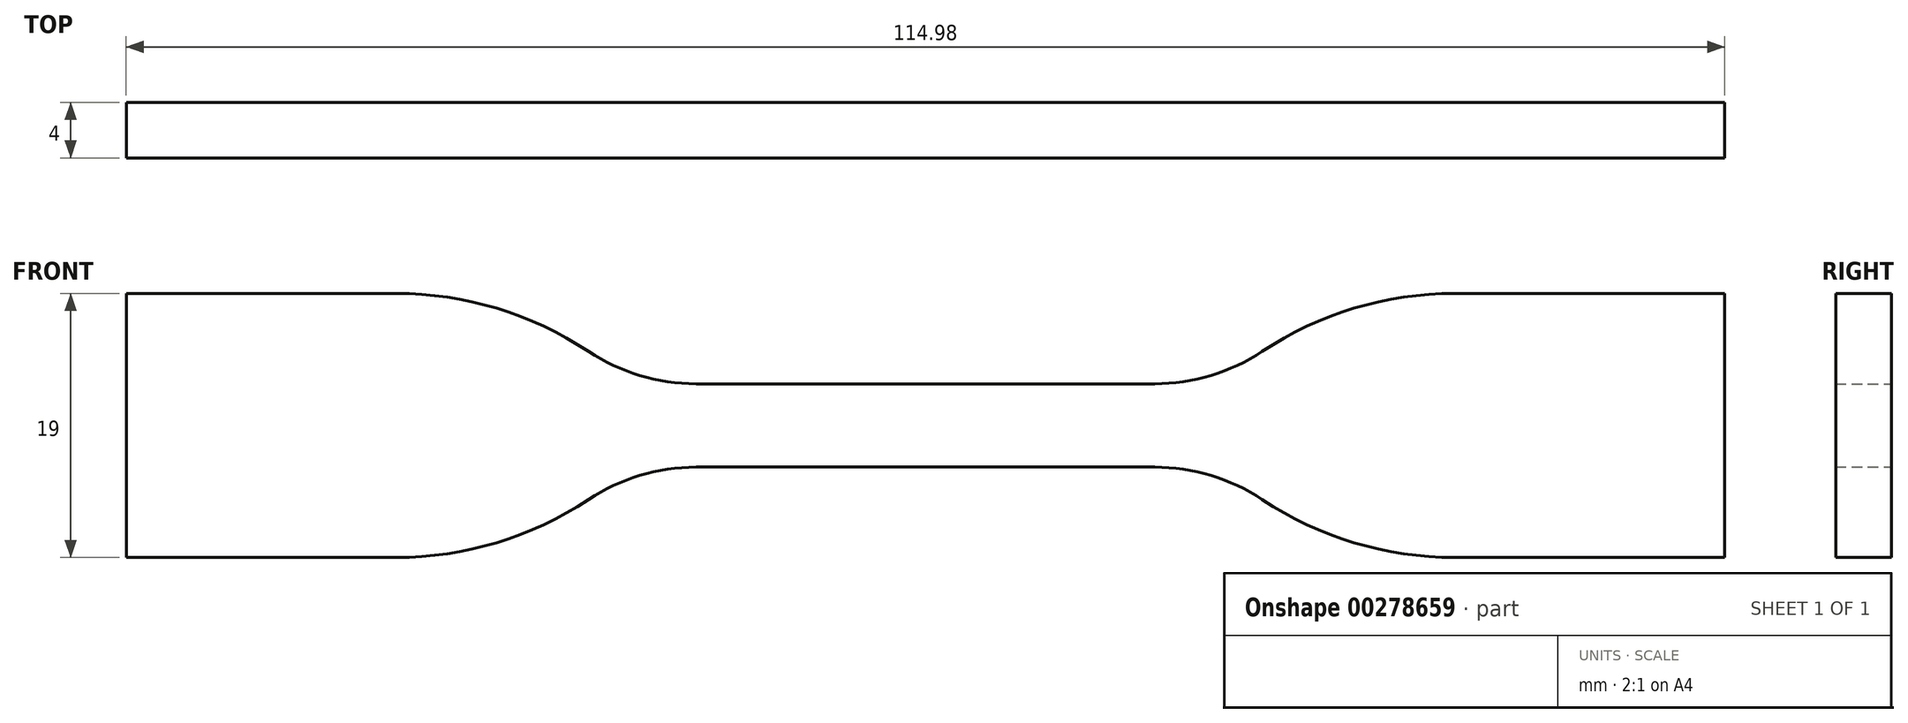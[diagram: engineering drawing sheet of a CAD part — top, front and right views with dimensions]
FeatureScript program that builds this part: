
annotation { "Feature Type Name" : "Feature", "Feature Type Description" : "" }
export const myFeature = defineFeature(function(context is Context, id is Id, definition is map)
    precondition{}
    {
        {
            var Q0;
            Q0=qCreatedBy(makeId("Front.planeOp"),FACE);
            var sketch = newSketch(context, id + "F0", { "sketchPlane" : qUnion([Q0])});
            skLineSegment(sketch, "E0", {"start": v(0, 3) * mm, "end": v(16.5, 3) * mm});
            skArc(sketch, "E1", {"start": v(16.5, 3) * mm, "mid": v(20.54, 3.6) * mm, "end": v(24.24, 5.33) * mm});
            skArc(sketch, "E2", {"start": v(24.24, 5.33) * mm, "mid": v(30.84, 8.43) * mm, "end": v(38.06, 9.5) * mm});
            skLineSegment(sketch, "E3", {"start": v(38.06, 9.5) * mm, "end": v(57.49, 9.5) * mm});
            skLineSegment(sketch, "E4.MirrorCS", {"start": v(0, -3) * mm, "end": v(16.5, -3) * mm});
            skLineSegment(sketch, "E5.MirrorCS", {"start": v(38.06, -9.5) * mm, "end": v(57.49, -9.5) * mm});
            skArc(sketch, "E6.MirrorCS", {"start": v(24.24, -5.33) * mm, "mid": v(30.84, -8.43) * mm, "end": v(38.06, -9.5) * mm});
            skArc(sketch, "E7.MirrorCS", {"start": v(16.5, -3) * mm, "mid": v(20.54, -3.6) * mm, "end": v(24.24, -5.33) * mm});
            skLineSegment(sketch, "E8.MirrorCS", {"start": v(0, -3) * mm, "end": v(-16.5, -3) * mm});
            skLineSegment(sketch, "E9.MirrorCS", {"start": v(0, 3) * mm, "end": v(-16.5, 3) * mm});
            skLineSegment(sketch, "E10.MirrorCS", {"start": v(-38.06, -9.5) * mm, "end": v(-57.49, -9.5) * mm});
            skLineSegment(sketch, "E11.MirrorCS", {"start": v(-38.06, 9.5) * mm, "end": v(-57.49, 9.5) * mm});
            skArc(sketch, "E12.MirrorCS", {"start": v(-16.5, -3) * mm, "mid": v(-20.54, -3.6) * mm, "end": v(-24.24, -5.33) * mm});
            skArc(sketch, "E13.MirrorCS", {"start": v(-24.24, 5.33) * mm, "mid": v(-30.84, 8.43) * mm, "end": v(-38.06, 9.5) * mm});
            skArc(sketch, "E14.MirrorCS", {"start": v(-24.24, -5.33) * mm, "mid": v(-30.84, -8.43) * mm, "end": v(-38.06, -9.5) * mm});
            skArc(sketch, "E15.MirrorCS", {"start": v(-16.5, 3) * mm, "mid": v(-20.54, 3.6) * mm, "end": v(-24.24, 5.33) * mm});
            skLineSegment(sketch, "E16", {"start": v(-57.49, 9.5) * mm, "end": v(-57.49, -9.5) * mm});
            skLineSegment(sketch, "E17", {"start": v(57.49, 9.5) * mm, "end": v(57.49, -9.5) * mm});
            skSolve(sketch);
        }
        {
            var Q0;
            Q0 = qSketchRegion(id + "F0", true);
            extrude(context, id + "F1", {"entities" : qUnion([Q0]), "depth" : 4 * mm});
        }
    });
